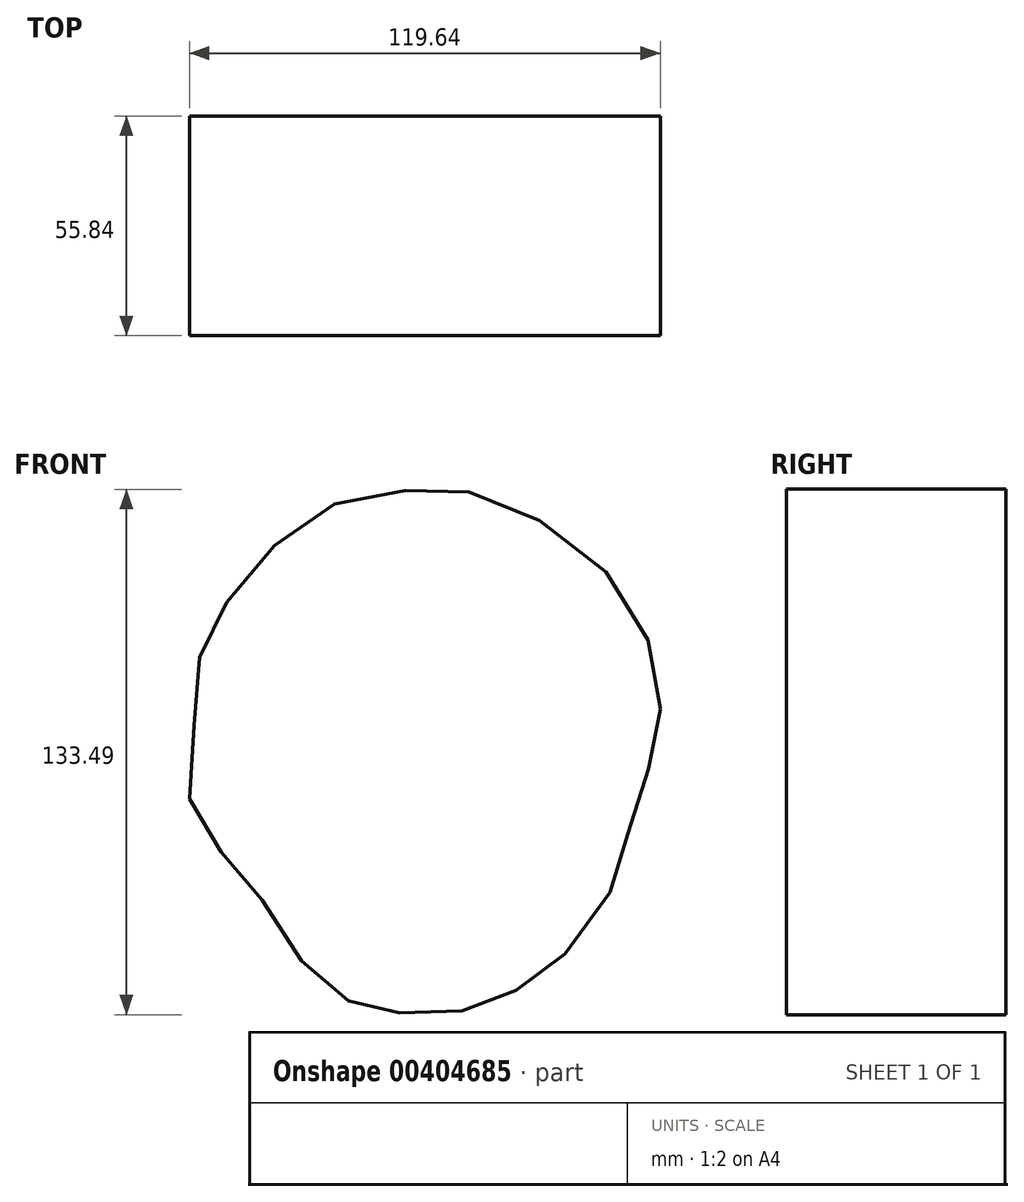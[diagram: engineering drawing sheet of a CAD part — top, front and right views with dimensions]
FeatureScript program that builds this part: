
annotation { "Feature Type Name" : "Feature", "Feature Type Description" : "" }
export const myFeature = defineFeature(function(context is Context, id is Id, definition is map)
    precondition{}
    {
        {
            var Q0;
            Q0=qCreatedBy(makeId("Front.planeOp"),FACE);
            var sketch = newSketch(context, id + "F0", { "sketchPlane" : qUnion([Q0])});
            skFitSpline(sketch, "E0", {"points": [v(-20.12, 62.86) * mm, v(-37.55, 50.2) * mm, v(-50.2, 33.82) * mm, v(-55.18, 20.54) * mm, v(-56.22, 0) * mm, v(-55.6, -18.46) * mm, v(-43.36, -30.5) * mm, v(-35.06, -44.19) * mm, v(-20.95, -60.78) * mm, v(-12.86, -64.52) * mm, v(0, -66.8) * mm, v(15.35, -65.14) * mm, v(27.18, -59.96) * mm, v(39.42, -50.41) * mm, v(51.66, -31.53) * mm, v(54.98, -18.05) * mm, v(61, 0) * mm, v(62.44, 13.9) * mm, v(56.64, 34.85) * mm, v(38.38, 54.56) * mm, v(15.77, 65.56) * mm, v(0, 66.39) * mm, v(-20.12, 62.86) * mm]});
            skSolve(sketch);
        }
        {
            var Q0;
            Q0=makeQuery(id+"F0.imprint","IMPRINT",FACE,{"disambiguationData":[TD([[makeQuery(id+"F0.imprint","IMPRINT",EDGE,{"derivedFrom":sQuery(id+"F0.wireOp",EDGE,"E0")}),1.0]])]});
            extrude(context, id + "F1", {"entities" : qUnion([Q0]), "depth" : 55.84 * mm});
        }
    });
